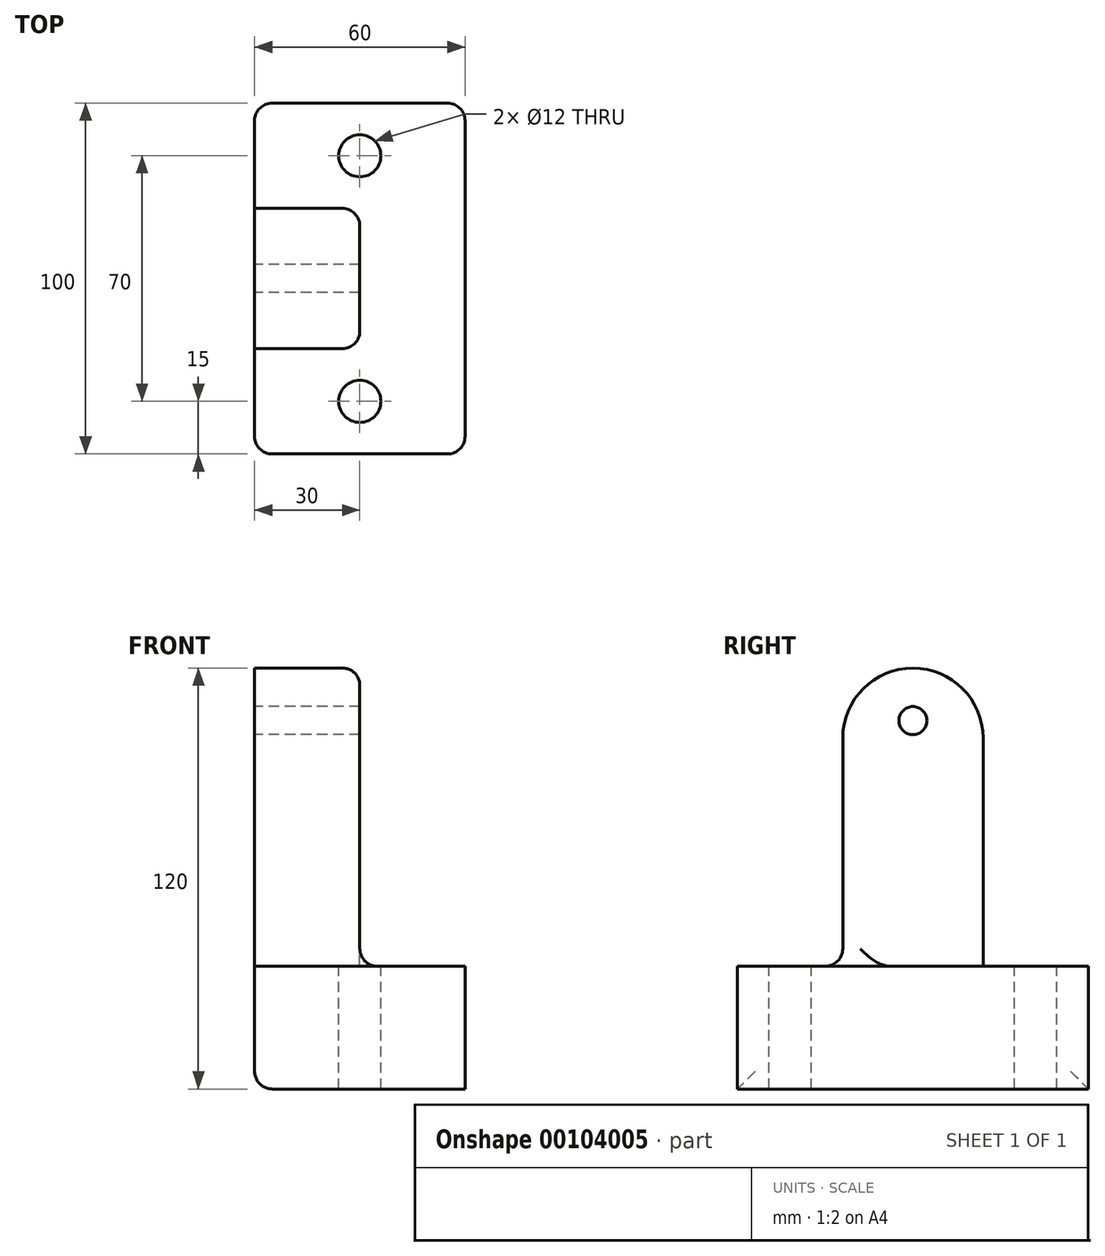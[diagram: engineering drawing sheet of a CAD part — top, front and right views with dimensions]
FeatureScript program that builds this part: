
annotation { "Feature Type Name" : "Feature", "Feature Type Description" : "" }
export const myFeature = defineFeature(function(context is Context, id is Id, definition is map)
    precondition{}
    {
        {
            var Q0;
            Q0=qCreatedBy(makeId("Top.planeOp"),FACE);
            var sketch = newSketch(context, id + "F0", { "sketchPlane" : qUnion([Q0])});
            skLineSegment(sketch, "E0.bottom", {"start": v(30, 50) * mm, "end": v(-30, 50) * mm});
            skLineSegment(sketch, "E0.top", {"start": v(30, -50) * mm, "end": v(-30, -50) * mm});
            skLineSegment(sketch, "E0.left", {"start": v(30, 50) * mm, "end": v(30, -50) * mm});
            skLineSegment(sketch, "E0.right", {"start": v(-30, 50) * mm, "end": v(-30, -50) * mm});
            skPoint(sketch, "E0.middle", {"position": v(0, 0) * mm});
            skSolve(sketch);
        }
        {
            var Q0;
            Q0=makeQuery(id+"F0.imprint","IMPRINT",FACE,{"disambiguationData":[TD([[makeQuery(id+"F0.imprint","IMPRINT",EDGE,{"derivedFrom":sQuery(id+"F0.wireOp",EDGE,"E0.bottom")}),1.0]])]});
            extrude(context, id + "F1", {"entities" : qUnion([Q0]), "depth" : 100 * mm});
        }
        {
            var Q0;
            Q0=makeQuery(id+"F1.opExtrude","CAP_FACE",FACE,{"disambiguationData":[OSD([sQuery(id+"F0.wireOp",EDGE,"E0.bottom"),sQuery(id+"F0.wireOp",EDGE,"E0.top"),sQuery(id+"F0.wireOp",EDGE,"E0.left"),sQuery(id+"F0.wireOp",EDGE,"E0.right")])],"isStart":false});
            var sketch = newSketch(context, id + "F2", { "sketchPlane" : qUnion([Q0])});
            skCircle(sketch, "E1", {"center": v(0, 35) * mm, "radius": 6 * mm});
            skCircle(sketch, "E2", {"center": v(0, -35) * mm, "radius": 6 * mm});
            skSolve(sketch);
        }
        {
            var Q0;
            Q0=makeQuery(id+"F2.imprint","IMPRINT",FACE,{"disambiguationData":[TD([[makeQuery(id+"F2.imprint","IMPRINT",EDGE,{"derivedFrom":sQuery(id+"F2.wireOp",EDGE,"E1")}),1.0]])]});
            var Q1;
            Q1=makeQuery(id+"F2.imprint","IMPRINT",FACE,{"disambiguationData":[TD([[makeQuery(id+"F2.imprint","IMPRINT",EDGE,{"derivedFrom":sQuery(id+"F2.wireOp",EDGE,"E2")}),1.0]])]});
            extrude(context, id + "F3", {"entities" : qUnion([Q0, Q1]), "operationType" : NewBodyOperationType.REMOVE, "oppositeDirection" : true, "depth" : 100 * mm});
        }
        {
            var Q0;
            Q0=makeQuery(id+"F1.opExtrude","CAP_FACE",FACE,{"disambiguationData":[OSD([sQuery(id+"F0.wireOp",EDGE,"E0.bottom"),sQuery(id+"F0.wireOp",EDGE,"E0.top"),sQuery(id+"F0.wireOp",EDGE,"E0.left"),sQuery(id+"F0.wireOp",EDGE,"E0.right")])],"isStart":false});
            var sketch = newSketch(context, id + "F4", { "sketchPlane" : qUnion([Q0])});
            skLineSegment(sketch, "E3", {"start": v(-30, 0) * mm, "end": v(0, 0) * mm});
            skLineSegment(sketch, "E4.top", {"start": v(-30, -20) * mm, "end": v(0, -20) * mm});
            skLineSegment(sketch, "E4.left", {"start": v(-30, 0) * mm, "end": v(-30, -20) * mm});
            skLineSegment(sketch, "E4.right", {"start": v(0, 0) * mm, "end": v(0, -20) * mm});
            skLineSegment(sketch, "E5.top", {"start": v(-30, 20) * mm, "end": v(0, 20) * mm});
            skLineSegment(sketch, "E5.left", {"start": v(-30, 0) * mm, "end": v(-30, 20) * mm});
            skLineSegment(sketch, "E5.right", {"start": v(0, 0) * mm, "end": v(0, 20) * mm});
            skSolve(sketch);
        }
        {
            var Q0;
            {var subQ4=sQuery(id+"F4.wireOp",EDGE,"E4.top");Q0=makeQuery(id+"F4.imprint","IMPRINT",FACE,{"disambiguationData":[TD([[makeQuery(id+"F4.imprint","IMPRINT",EDGE,{"derivedFrom":subQ4}),-1.0]])]});}
            extrude(context, id + "F5", {"entities" : qUnion([Q0]), "operationType" : NewBodyOperationType.REMOVE, "oppositeDirection" : true, "depth" : 65 * mm});
        }
        {
            var Q0;
            Q0=makeQuery(id+"F1.opExtrude","CAP_FACE",FACE,{"disambiguationData":[OSD([sQuery(id+"F0.wireOp",EDGE,"E0.bottom"),sQuery(id+"F0.wireOp",EDGE,"E0.top"),sQuery(id+"F0.wireOp",EDGE,"E0.left"),sQuery(id+"F0.wireOp",EDGE,"E0.right")])],"isStart":false});
            var sketch = newSketch(context, id + "F6", { "sketchPlane" : qUnion([Q0])});
            skLineSegment(sketch, "E6", {"start": v(-30, 0) * mm, "end": v(0, 0) * mm});
            skSolve(sketch);
        }
        {
            var Q0;
            {var subQ0=sQuery(id+"F6.wireOp",EDGE,"E6");Q0=makeQuery(id+"F6.imprint","IMPRINT",FACE,{"disambiguationData":[TD([[makeQuery(id+"F6.imprint","IMPRINT",EDGE,{"derivedFrom":subQ0}),-1.0]])]});}
            var Q1;
            Q1=sQuery(id+"F6.wireOp",EDGE,"E6");
            revolve(context, id + "F7", {"operationType" : NewBodyOperationType.ADD, "entities" : qUnion([Q0]), "axis" : qUnion([Q1]), "revolveType" : RevolveType.ONE_DIRECTION, "oppositeDirection" : true, "angle" : 180 * degree});
        }
        {
            var Q0;
            {var subQ0=sQuery(id+"F0.wireOp",EDGE,"E0.right");Q0=makeQuery(id+"F7.boolean.opBoolean","MERGE",FACE,{"derivedFrom":[makeQuery(id+"F1.opExtrude","SWEPT_FACE",FACE,{"disambiguationData":[OSD([subQ0])]}),makeQuery(id+"F7.opRevolve","SWEPT_FACE",FACE,{"disambiguationData":[OSD([subQ0])]})]});}
            var sketch = newSketch(context, id + "F8", { "sketchPlane" : qUnion([Q0])});
            skCircle(sketch, "E7", {"center": v(0, 105) * mm, "radius": 4 * mm});
            skSolve(sketch);
        }
        {
            var Q0;
            Q0=makeQuery(id+"F8.imprint","IMPRINT",FACE,{"disambiguationData":[TD([[makeQuery(id+"F8.imprint","IMPRINT",EDGE,{"derivedFrom":sQuery(id+"F8.wireOp",EDGE,"E7")}),1.0]])]});
            extrude(context, id + "F9", {"entities" : qUnion([Q0]), "operationType" : NewBodyOperationType.REMOVE, "oppositeDirection" : true, "depth" : 50 * mm});
        }
        {
            var Q0;
            Q0=makeQuery(id+"F5.boolean.opBoolean","COPY",EDGE,{"derivedFrom":makeQuery(id+"F5.opExtrude","SWEPT_EDGE",EDGE,{"disambiguationData":[OSD([sQuery(id+"F0.wireOp",EDGE,"E0.right"),sQuery(id+"F4.wireOp",EDGE,"E5.top"),sQuery(id+"F4.wireOp",EDGE,"E5.left")])]})});
            var Q1;
            {var subQ0=sQuery(id+"F0.wireOp",EDGE,"E0.right");var subQ1=makeQuery(id+"F1.opExtrude","CAP_EDGE",EDGE,{"disambiguationData":[OSD([subQ0])],"isStart":false});Q1=makeQuery(id+"F5.boolean.opBoolean","COPY",EDGE,{"derivedFrom":makeQuery(id+"F5.opExtrude","CAP_EDGE",EDGE,{"disambiguationData":[OSD([subQ0]),TDD([makeQuery(id+"F4.imprint","IMPRINT",EDGE,{"disambiguationData":[TD([[makeQuery(id+"F4.imprint","INTERSECT",VERTEX,{"derivedFrom":[makeQuery(id+"F1.opExtrude","CAP_EDGE",EDGE,{"disambiguationData":[OSD([sQuery(id+"F0.wireOp",EDGE,"E0.bottom")])],"isStart":false}),subQ1]}),-1.0]])],"derivedFrom":subQ1})])],"isStart":false})});}
            var Q2;
            Q2=makeQuery(id+"F1.opExtrude","SWEPT_EDGE",EDGE,{"disambiguationData":[OSD([sQuery(id+"F0.wireOp",EDGE,"E0.bottom"),sQuery(id+"F0.wireOp",EDGE,"E0.right")])]});
            var Q3;
            Q3=makeQuery(id+"F1.opExtrude","CAP_EDGE",EDGE,{"disambiguationData":[OSD([sQuery(id+"F0.wireOp",EDGE,"E0.right")])],"isStart":true});
            var Q4;
            {var subQ0=sQuery(id+"F0.wireOp",EDGE,"E0.right");var subQ1=makeQuery(id+"F1.opExtrude","CAP_EDGE",EDGE,{"disambiguationData":[OSD([subQ0])],"isStart":false});Q4=makeQuery(id+"F5.boolean.opBoolean","COPY",EDGE,{"derivedFrom":makeQuery(id+"F5.opExtrude","CAP_EDGE",EDGE,{"disambiguationData":[OSD([subQ0]),TDD([makeQuery(id+"F4.imprint","IMPRINT",EDGE,{"disambiguationData":[TD([[makeQuery(id+"F4.imprint","INTERSECT",VERTEX,{"derivedFrom":[makeQuery(id+"F1.opExtrude","CAP_EDGE",EDGE,{"disambiguationData":[OSD([sQuery(id+"F0.wireOp",EDGE,"E0.top")])],"isStart":false}),subQ1]}),1.0]])],"derivedFrom":subQ1})])],"isStart":false})});}
            var Q5;
            Q5=makeQuery(id+"F1.opExtrude","SWEPT_EDGE",EDGE,{"disambiguationData":[OSD([sQuery(id+"F0.wireOp",EDGE,"E0.top"),sQuery(id+"F0.wireOp",EDGE,"E0.right")])]});
            var Q6;
            Q6=makeQuery(id+"F5.boolean.opBoolean","COPY",EDGE,{"derivedFrom":makeQuery(id+"F5.opExtrude","CAP_EDGE",EDGE,{"disambiguationData":[OSD([sQuery(id+"F0.wireOp",EDGE,"E0.top")])],"isStart":false})});
            var Q7;
            Q7=makeQuery(id+"F1.opExtrude","SWEPT_EDGE",EDGE,{"disambiguationData":[OSD([sQuery(id+"F0.wireOp",EDGE,"E0.top"),sQuery(id+"F0.wireOp",EDGE,"E0.left")])]});
            var Q8;
            Q8=makeQuery(id+"F5.boolean.opBoolean","COPY",EDGE,{"derivedFrom":makeQuery(id+"F5.opExtrude","CAP_EDGE",EDGE,{"disambiguationData":[OSD([sQuery(id+"F0.wireOp",EDGE,"E0.left")])],"isStart":false})});
            var Q9;
            Q9=makeQuery(id+"F5.boolean.opBoolean","COPY",EDGE,{"derivedFrom":makeQuery(id+"F5.opExtrude","CAP_EDGE",EDGE,{"disambiguationData":[OSD([sQuery(id+"F4.wireOp",EDGE,"E4.top")])],"isStart":false})});
            var Q10;
            Q10=makeQuery(id+"F5.boolean.opBoolean","COPY",EDGE,{"derivedFrom":makeQuery(id+"F5.opExtrude","SWEPT_EDGE",EDGE,{"disambiguationData":[OSD([sQuery(id+"F4.wireOp",EDGE,"E4.top"),sQuery(id+"F4.wireOp",EDGE,"E4.right")])]})});
            var Q11;
            Q11=makeQuery(id+"F1.opExtrude","SWEPT_EDGE",EDGE,{"disambiguationData":[OSD([sQuery(id+"F0.wireOp",EDGE,"E0.bottom"),sQuery(id+"F0.wireOp",EDGE,"E0.left")])]});
            var Q12;
            Q12=makeQuery(id+"F5.boolean.opBoolean","COPY",EDGE,{"derivedFrom":makeQuery(id+"F5.opExtrude","CAP_EDGE",EDGE,{"disambiguationData":[OSD([sQuery(id+"F0.wireOp",EDGE,"E0.bottom")])],"isStart":false})});
            fillet(context, id + "F10", {"entities" : qUnion([Q0, Q1, Q2, Q3, Q4, Q5, Q6, Q7, Q8, Q9, Q10, Q11, Q12]), "radius" : 5 * mm, "tangentPropagation" : true, "allowEdgeOverflow" : false});
        }
    });
